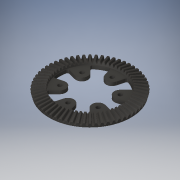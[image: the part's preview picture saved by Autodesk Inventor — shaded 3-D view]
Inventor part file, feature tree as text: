
AUTODESK INVENTOR PART (.ipt)
format: ipt  version: 2019.3 (Build 233278000, 278)  size: 2,841,600 bytes
history: native  units: in
note: dims shown in document units (in); Inventor stores cm internally (conversion verified against a paired STEP export)
features: sketch x3, extrude x2, hole x1, fillet x1, imported_body x1
ambient origin geometry x8: Origin, YZ Plane, XZ Plane, XY Plane, X Axis, Y Axis, Z Axis, Center Point
bodies: Solid1 (feature_tree)
feature tree (8):
  extrude  "Extrusion1"  Depth=0.9375in
  hole  "Hole1"  [1 undecoded]
  extrude  "Extrusion2"  Depth=0.0625in TaperAngle=360.0deg
  fillet  "Fillet1"  [1 undecoded]
  sketch  "Sketch1"  dims[d0=0.685in d1=0.0in d2=0.9375in]
  sketch  "Sketch2"  dims[d3=2.3622in d5=360.0deg]
  sketch  "Sketch3"  dims[d7=0.17in d8=0.2362in d9=0.1575in d10=0.0787in d11=90.0deg d12=0.315in d13=0.8108in d15=0.5in d21=2.3622in d23=360.0deg d25=0.0in d26=0.0in d27=0.0625in]
  imported_body  "Base1"
note: 2 required parameter values undecoded (feature->parameter linkage not recoverable at this tier; creation-order binding heuristic only, values carry confidence <= 0.55)
